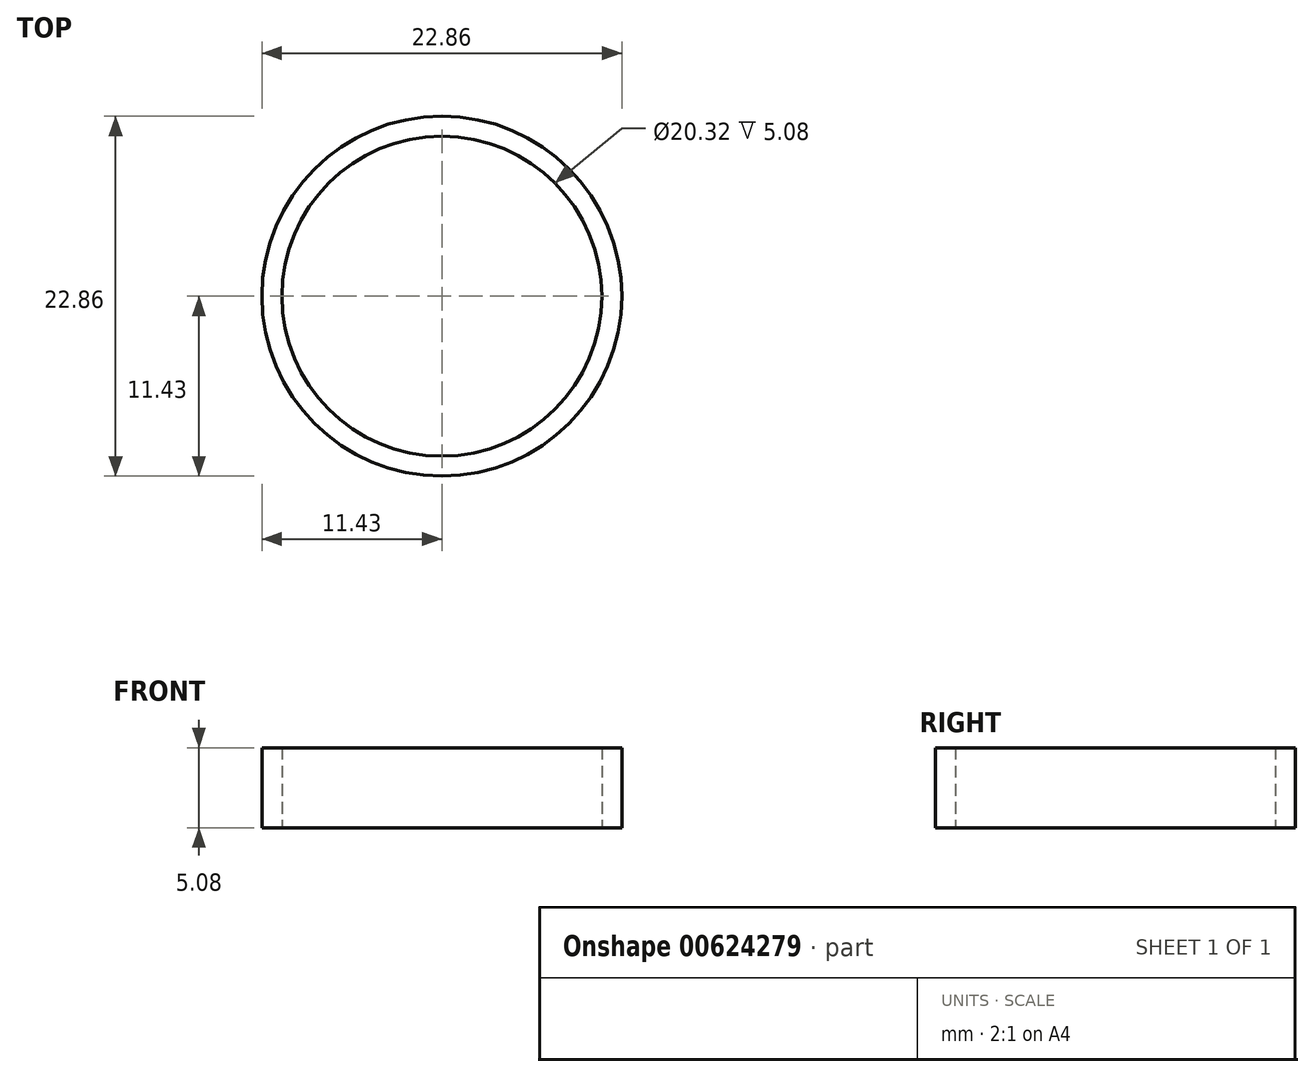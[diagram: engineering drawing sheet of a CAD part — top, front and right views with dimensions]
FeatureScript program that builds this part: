
annotation { "Feature Type Name" : "Feature", "Feature Type Description" : "" }
export const myFeature = defineFeature(function(context is Context, id is Id, definition is map)
    precondition{}
    {
        {
            var Q0;
            Q0=qCreatedBy(makeId("Top.planeOp"),FACE);
            var sketch = newSketch(context, id + "F0", { "sketchPlane" : qUnion([Q0])});
            skCircle(sketch, "E0", {"center": v(0, 0) * mm, "radius": 10.16 * mm});
            skCircle(sketch, "E1", {"center": v(0, 0) * mm, "radius": 11.43 * mm});
            skSolve(sketch);
        }
        {
            var Q0;
            Q0 = qSketchRegion(id + "F0", true);
            extrude(context, id + "F1", {"entities" : qUnion([Q0]), "depth" : 5.08 * mm, "offsetDistance" : 25.4 * mm});
        }
    });
